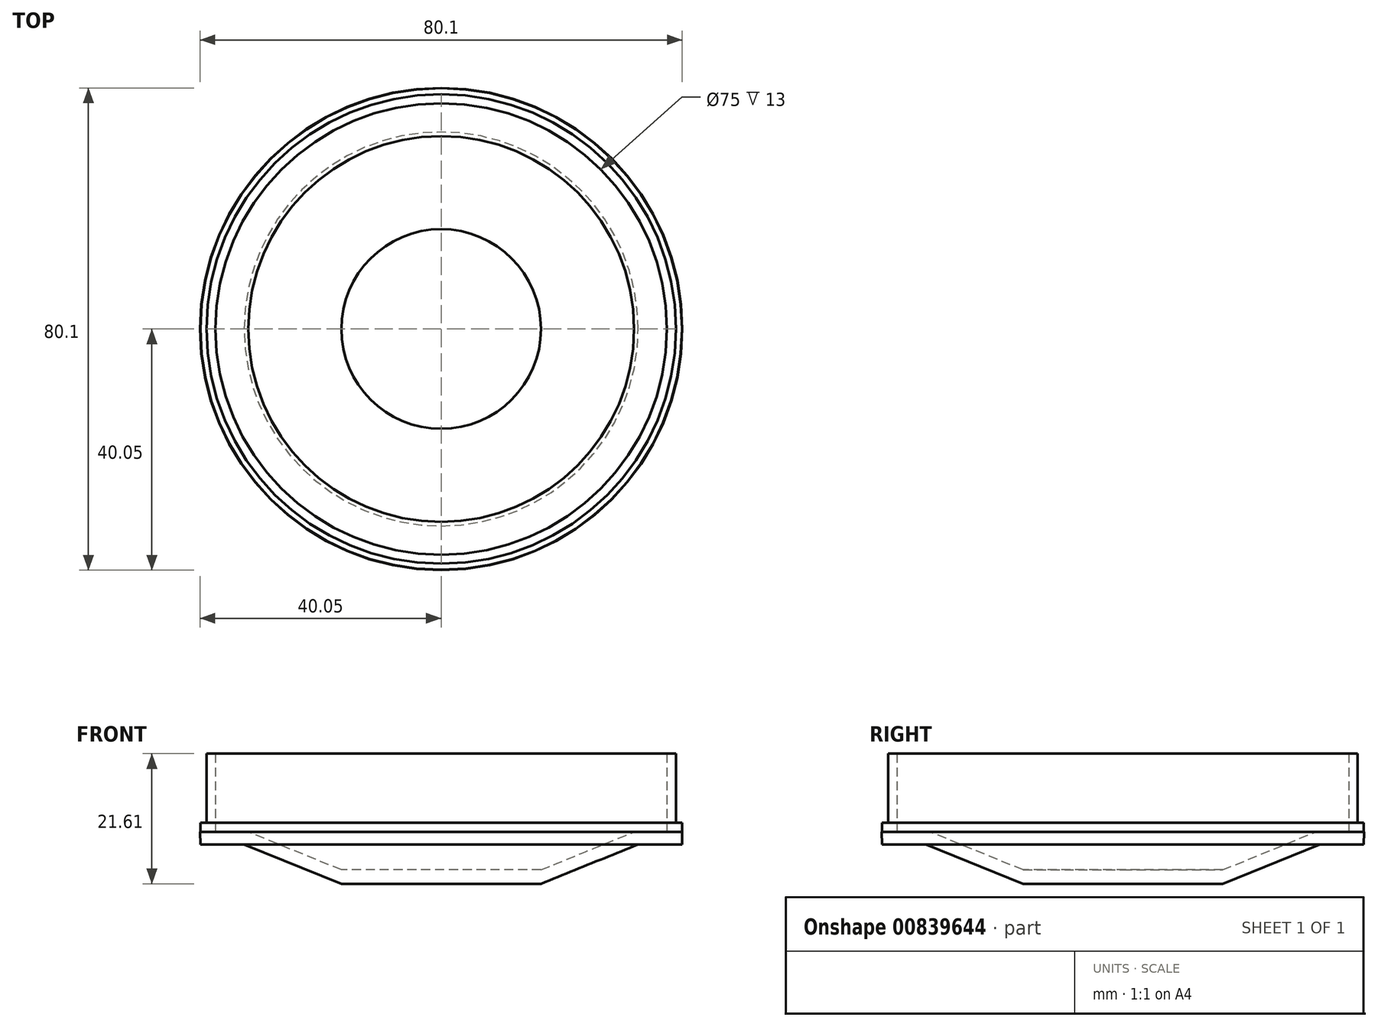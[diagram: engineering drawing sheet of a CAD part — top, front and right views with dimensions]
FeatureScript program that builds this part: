
annotation { "Feature Type Name" : "Feature", "Feature Type Description" : "" }
export const myFeature = defineFeature(function(context is Context, id is Id, definition is map)
    precondition{}
    {
        {
            var Q0;
            Q0=qCreatedBy(makeId("Top.planeOp"),FACE);
            var sketch = newSketch(context, id + "F0", { "sketchPlane" : qUnion([Q0])});
            skCircle(sketch, "E0", {"center": v(0, 0) * mm, "radius": 37.5 * mm});
            skCircle(sketch, "E1", {"center": v(0, 0) * mm, "radius": 39 * mm});
            skSolve(sketch);
        }
        {
            var Q0;
            Q0=makeQuery(id+"F0.imprint","IMPRINT",FACE,{"disambiguationData":[TD([[makeQuery(id+"F0.imprint","IMPRINT",EDGE,{"derivedFrom":sQuery(id+"F0.wireOp",EDGE,"E0")}),-1.0]])]});
            extrude(context, id + "F1", {"entities" : qUnion([Q0]), "depth" : 13 * mm, "offsetDistance" : 25 * mm});
        }
        {
            var Q0;
            Q0=qCreatedBy(makeId("Top.planeOp"),FACE);
            var sketch = newSketch(context, id + "F2", { "sketchPlane" : qUnion([Q0])});
            skCircle(sketch, "E2", {"center": v(0, 0) * mm, "radius": 37.5 * mm});
            skCircle(sketch, "E3", {"center": v(0, 0) * mm, "radius": 40 * mm});
            skSolve(sketch);
        }
        {
            var Q0;
            Q0 = qSketchRegion(id + "F2", true);
            extrude(context, id + "F3", {"entities" : qUnion([Q0]), "operationType" : NewBodyOperationType.ADD, "endBound" : BoundingType.SYMMETRIC, "depth" : 3 * mm, "offsetDistance" : 25 * mm});
        }
        {
            var Q0;
            Q0=qCreatedBy(makeId("Right.planeOp"),FACE);
            var sketch = newSketch(context, id + "F4", { "sketchPlane" : qUnion([Q0])});
            skLineSegment(sketch, "E4", {"start": v(40.05, 0) * mm, "end": v(32.04, 0) * mm});
            skLineSegment(sketch, "E5", {"start": v(32.04, 0) * mm, "end": v(16.58, -6.3) * mm});
            skLineSegment(sketch, "E6", {"start": v(16.58, -6.3) * mm, "end": v(0, -6.3) * mm});
            skLineSegment(sketch, "E7", {"start": v(0, -6.3) * mm, "end": v(0, -8.61) * mm});
            skLineSegment(sketch, "E8", {"start": v(0, -8.61) * mm, "end": v(16.57, -8.61) * mm});
            skLineSegment(sketch, "E9", {"start": v(16.57, -8.61) * mm, "end": v(32.72, -2.08) * mm});
            skLineSegment(sketch, "E10", {"start": v(32.72, -2.08) * mm, "end": v(40, -2.08) * mm});
            skLineSegment(sketch, "E11", {"start": v(40, -2.08) * mm, "end": v(40.05, 0) * mm});
            skSolve(sketch);
        }
        {
            var Q0;
            Q0=makeQuery(id+"F4.imprint","IMPRINT",FACE,{"disambiguationData":[TD([[makeQuery(id+"F4.imprint","IMPRINT",EDGE,{"derivedFrom":sQuery(id+"F4.wireOp",EDGE,"E4")}),1.0]])]});
            var Q1;
            Q1=sQuery(id+"F4.wireOp",EDGE,"E7");
            revolve(context, id + "F5", {"operationType" : NewBodyOperationType.ADD, "surfaceOperationType" : NewSurfaceOperationType.NEW, "entities" : qUnion([Q0]), "axis" : qUnion([Q1]), "revolveType" : RevolveType.FULL});
        }
    });
